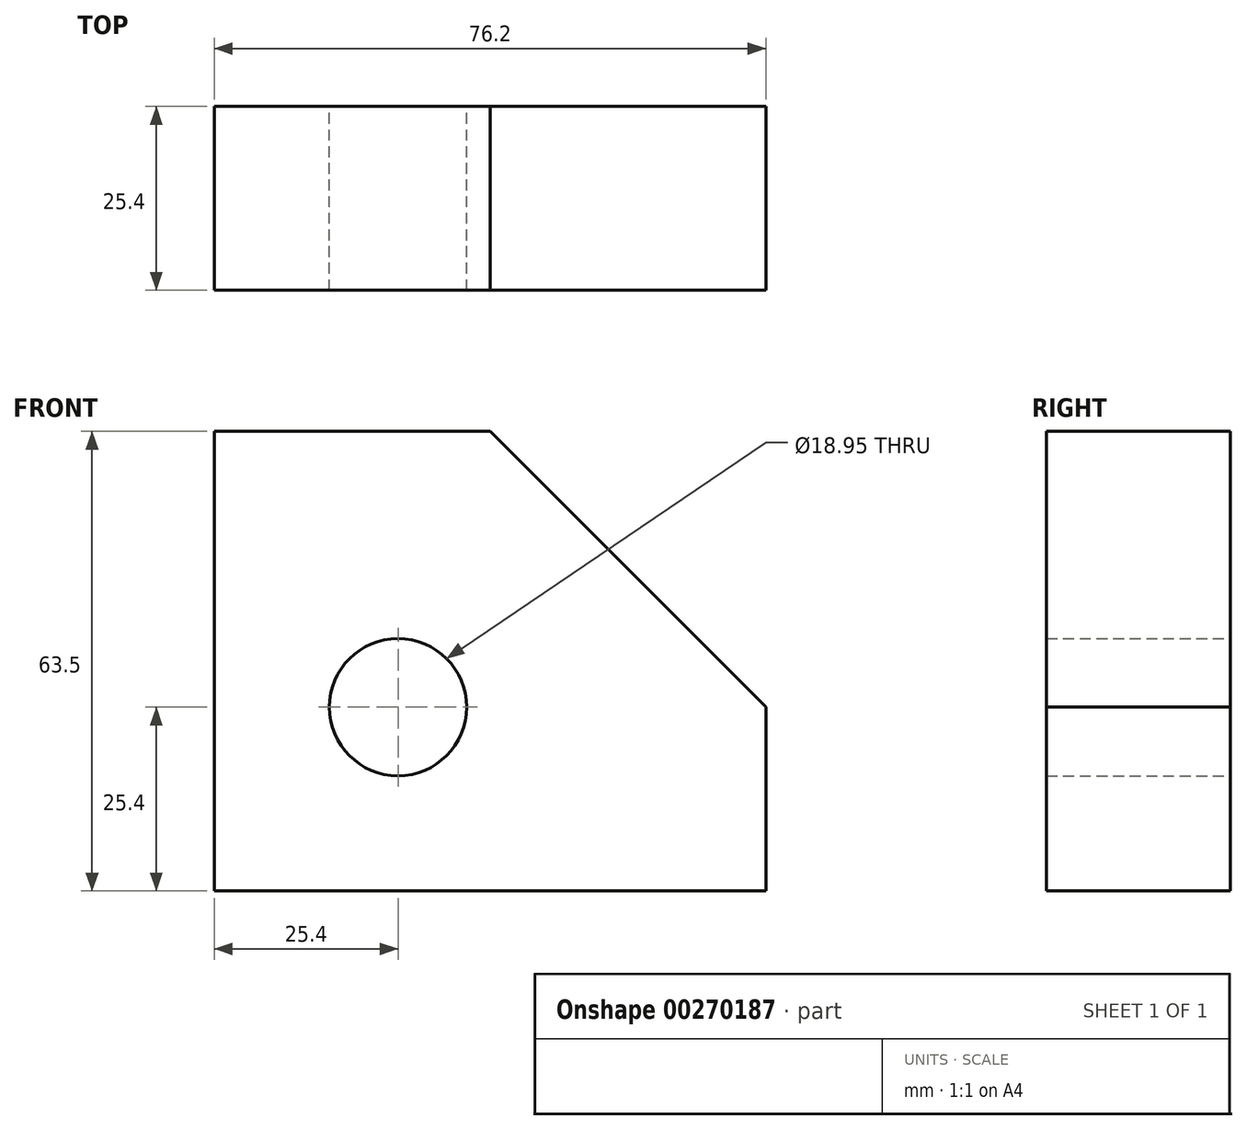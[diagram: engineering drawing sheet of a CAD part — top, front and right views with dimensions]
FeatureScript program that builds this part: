
annotation { "Feature Type Name" : "Feature", "Feature Type Description" : "" }
export const myFeature = defineFeature(function(context is Context, id is Id, definition is map)
    precondition{}
    {
        {
            var Q0;
            Q0=qCreatedBy(makeId("Front.planeOp"),FACE);
            var sketch = newSketch(context, id + "F0", { "sketchPlane" : qUnion([Q0])});
            skLineSegment(sketch, "E0", {"start": v(0, 0) * mm, "end": v(76.2, 0) * mm});
            skLineSegment(sketch, "E1", {"start": v(76.2, 0) * mm, "end": v(76.2, 25.4) * mm});
            skLineSegment(sketch, "E2", {"start": v(76.2, 25.4) * mm, "end": v(38.1, 63.5) * mm});
            skLineSegment(sketch, "E3", {"start": v(38.1, 63.5) * mm, "end": v(0, 63.5) * mm});
            skLineSegment(sketch, "E4", {"start": v(0, 63.5) * mm, "end": v(0, 0) * mm});
            skCircle(sketch, "E5", {"center": v(25.4, 25.4) * mm, "radius": 9.47 * mm});
            skSolve(sketch);
        }
        {
            var Q0;
            Q0=makeQuery(id+"F0.imprint","IMPRINT",FACE,{"disambiguationData":[TD([[makeQuery(id+"F0.imprint","IMPRINT",EDGE,{"derivedFrom":sQuery(id+"F0.wireOp",EDGE,"E0")}),1.0]])]});
            extrude(context, id + "F1", {"entities" : qUnion([Q0]), "depth" : 25.4 * mm, "symmetric" : true});
        }
    });
